# Revit family: Lighting_Linear_LED_StarTek_StarPower-Rotational-Mount1
name_source: partatom
category: Lighting Fixtures
units: mm (PartAtom-declared; Revit-internal decimal feet)

## family parameters
Cut with Voids When Loaded = No
Host = Face
Light Source = No
OmniClass Number = 23.80.70.11
OmniClass Title = Luminaries for Internal Lighting
Part Type = Normal
Room Calculation Point = No
Round Connector Dimension = Use Diameter
Shared = No

## types (1)
- Not a type - Load Type Catalog!
    Apparent Load = 35 VA
    Assembly Code = D5020200
    CRI = 80
    Default Elevation = 48 "
    Description = StarPower
    Distribution = SD
    Frequency = 60 Hz
    Height = 2.9 "
    Input Wattage = 33 W
    Keynote = 16500
    Lamp = LED
    Length = 48 "
    Manufacturer = StarTek Lighting
    Model = StarPower
    Number of Poles = 1
    Output = High
    Phase = 1
    Photometric Note = Import IES files https://starteklightingamerica.com
    Photometric Option = Light-Source_StarTek_StarPower-Rotational-Mount : Not a Type - Load Type Catalog!
    Photometric Web File Note = Please remember to reload the shared light file with the type catalog for all available light options and link the proper .ies file to the shared file.
    Power Factor = 0.93
    Product data url = https://www.bimobject.com
    Type Comments = Linear Lighting Fixture
    URL = https://starteklightingamerica.com
    Voltage = 120 V
    Voltage Range = 120-277V
    Wattage Comments = Efficacy up to 145 lm/W
    Weight = 8.00 lbf
    Width = 2.5 "

## geometry (parser evidence)
native form markers: Sweep x8
no freeform markers — native parametric forms only
